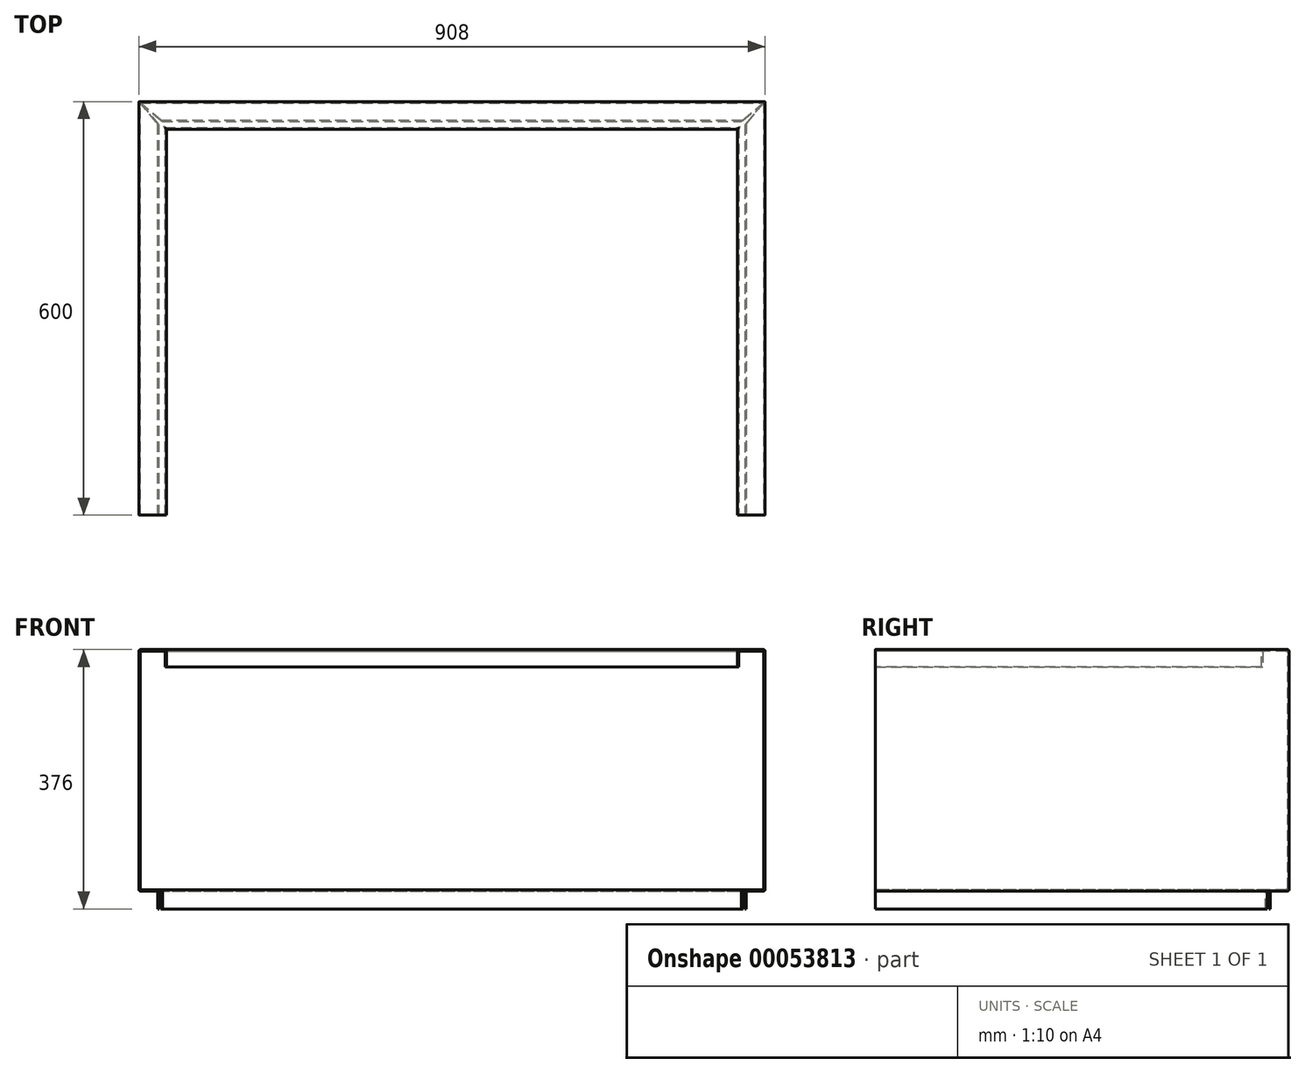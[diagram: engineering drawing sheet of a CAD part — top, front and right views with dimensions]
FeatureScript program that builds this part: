
annotation { "Feature Type Name" : "Feature", "Feature Type Description" : "" }
export const myFeature = defineFeature(function(context is Context, id is Id, definition is map)
    precondition{}
    {
        {
            var Q0;
            Q0=qCreatedBy(makeId("Front.planeOp"),FACE);
            var sketch = newSketch(context, id + "F0", { "sketchPlane" : qUnion([Q0])});
            skLineSegment(sketch, "E0", {"start": v(40, -25) * mm, "end": v(40, 0) * mm});
            skLineSegment(sketch, "E1", {"start": v(40, 0) * mm, "end": v(0, 0) * mm});
            skLineSegment(sketch, "E2", {"start": v(0, 0) * mm, "end": v(0, -350) * mm});
            skLineSegment(sketch, "E3", {"start": v(0, -350) * mm, "end": v(27, -350) * mm});
            skLineSegment(sketch, "E4", {"start": v(27, -350) * mm, "end": v(27, -376) * mm});
            skLineSegment(sketch, "E5.0", {"start": v(29, -348) * mm, "end": v(29, -376) * mm});
            skLineSegment(sketch, "E5.1", {"start": v(38, -25) * mm, "end": v(38, -2) * mm});
            skLineSegment(sketch, "E5.2", {"start": v(38, -2) * mm, "end": v(2, -2) * mm});
            skLineSegment(sketch, "E5.3", {"start": v(2, -2) * mm, "end": v(2, -348) * mm});
            skLineSegment(sketch, "E5.4", {"start": v(2, -348) * mm, "end": v(29, -348) * mm});
            skLineSegment(sketch, "E6", {"start": v(38, -25) * mm, "end": v(40, -25) * mm});
            skLineSegment(sketch, "E7", {"start": v(27, -376) * mm, "end": v(29, -376) * mm});
            skSolve(sketch);
        }
        {
            var Q0;
            Q0=qCreatedBy(makeId("Top.planeOp"),FACE);
            var sketch = newSketch(context, id + "F1", { "sketchPlane" : qUnion([Q0])});
            skLineSegment(sketch, "E8", {"start": v(0, 0) * mm, "end": v(0, 600) * mm});
            skLineSegment(sketch, "E9", {"start": v(0, 600) * mm, "end": v(908, 600) * mm});
            skLineSegment(sketch, "E10", {"start": v(908, 600) * mm, "end": v(908, 0) * mm});
            skSolve(sketch);
        }
        {
            var Q0;
            Q0 = qSketchRegion(id + "F0", true);
            var Q1;
            Q1 = qConstructionFilter(qBodyType(qCreatedBy(id + "F1" ,EDGE), BodyType.WIRE), ConstructionObject.NO);
            sweep(context, id + "F2", {"profiles" : qUnion([Q0]), "path" : qUnion([Q1])});
        }
        {
            var Q0;
            Q0=makeQuery(id+"F2.opSweep","SWEPT_FACE",FACE,{"disambiguationData":[OSD([sQuery(id+"F0.wireOp",EDGE,"E5.4"),sQuery(id+"F1.wireOp",EDGE,"E8")])]});
            var sketch = newSketch(context, id + "F3", { "sketchPlane" : qUnion([Q0])});
            skLineSegment(sketch, "E11", {"start": v(2, 598) * mm, "end": v(29, 565.82) * mm});
            skLineSegment(sketch, "E12", {"start": v(29, 565.82) * mm, "end": v(34.18, 571) * mm});
            skLineSegment(sketch, "E13", {"start": v(34.18, 571) * mm, "end": v(2, 598) * mm});
            skLineSegment(sketch, "E14", {"start": v(906, 598) * mm, "end": v(879, 565.82) * mm});
            skLineSegment(sketch, "E15", {"start": v(879, 565.82) * mm, "end": v(873.82, 571) * mm});
            skLineSegment(sketch, "E16", {"start": v(873.82, 571) * mm, "end": v(906, 598) * mm});
            skSolve(sketch);
        }
        {
            var Q0;
            {var subQ0=sQuery(id+"F3.wireOp",EDGE,"E14");Q0=makeQuery(id+"F3.imprint","IMPRINT",FACE,{"disambiguationData":[TD([[makeQuery(id+"F3.imprint","IMPRINT",EDGE,{"derivedFrom":subQ0}),-1.0]])]});}
            var Q1;
            {var subQ0=sQuery(id+"F3.wireOp",EDGE,"E11");Q1=makeQuery(id+"F3.imprint","IMPRINT",FACE,{"disambiguationData":[TD([[makeQuery(id+"F3.imprint","IMPRINT",EDGE,{"derivedFrom":subQ0}),1.0]])]});}
            extrude(context, id + "F4", {"entities" : qUnion([Q0, Q1]), "operationType" : NewBodyOperationType.REMOVE, "oppositeDirection" : true, "depth" : 30 * mm});
        }
        {
            var Q0;
            Q0=makeQuery(id+"F2.opSweep","SWEPT_EDGE",EDGE,{"disambiguationData":[OSD([sQuery(id+"F0.wireOp",EDGE,"E0"),sQuery(id+"F0.wireOp",EDGE,"E1"),sQuery(id+"F1.wireOp",EDGE,"E8")])]});
            var Q1;
            Q1=makeQuery(id+"F2.opSweep","SWEPT_EDGE",EDGE,{"disambiguationData":[OSD([sQuery(id+"F0.wireOp",EDGE,"E1"),sQuery(id+"F0.wireOp",EDGE,"E2"),sQuery(id+"F1.wireOp",EDGE,"E8")])]});
            var Q2;
            Q2=makeQuery(id+"F2.opSweep","SWEPT_EDGE",EDGE,{"disambiguationData":[OSD([sQuery(id+"F0.wireOp",EDGE,"E1"),sQuery(id+"F0.wireOp",EDGE,"E2"),sQuery(id+"F1.wireOp",EDGE,"E9")])]});
            var Q3;
            Q3=makeQuery(id+"F2.opSweep","SWEPT_EDGE",EDGE,{"disambiguationData":[OSD([sQuery(id+"F0.wireOp",EDGE,"E0"),sQuery(id+"F0.wireOp",EDGE,"E1"),sQuery(id+"F1.wireOp",EDGE,"E9")])]});
            var Q4;
            Q4=makeQuery(id+"F2.opSweep","SWEPT_EDGE",EDGE,{"disambiguationData":[OSD([sQuery(id+"F0.wireOp",EDGE,"E0"),sQuery(id+"F0.wireOp",EDGE,"E1"),sQuery(id+"F1.wireOp",EDGE,"E10")])]});
            var Q5;
            Q5=makeQuery(id+"F2.opSweep","SWEPT_EDGE",EDGE,{"disambiguationData":[OSD([sQuery(id+"F0.wireOp",EDGE,"E1"),sQuery(id+"F0.wireOp",EDGE,"E2"),sQuery(id+"F1.wireOp",EDGE,"E10")])]});
            var Q6;
            Q6=makeQuery(id+"F2.opSweep","SWEPT_EDGE",EDGE,{"disambiguationData":[OSD([sQuery(id+"F0.wireOp",EDGE,"E5.0"),sQuery(id+"F0.wireOp",EDGE,"E5.4"),sQuery(id+"F1.wireOp",EDGE,"E8")])]});
            var Q7;
            Q7=makeQuery(id+"F2.opSweep","SWEPT_EDGE",EDGE,{"disambiguationData":[OSD([sQuery(id+"F0.wireOp",EDGE,"E5.3"),sQuery(id+"F0.wireOp",EDGE,"E5.4"),sQuery(id+"F1.wireOp",EDGE,"E8")])]});
            var Q8;
            Q8=makeQuery(id+"F2.opSweep","SWEPT_EDGE",EDGE,{"disambiguationData":[OSD([sQuery(id+"F0.wireOp",EDGE,"E5.3"),sQuery(id+"F0.wireOp",EDGE,"E5.4"),sQuery(id+"F1.wireOp",EDGE,"E9")])]});
            var Q9;
            Q9=makeQuery(id+"F2.opSweep","SWEPT_EDGE",EDGE,{"disambiguationData":[OSD([sQuery(id+"F0.wireOp",EDGE,"E5.0"),sQuery(id+"F0.wireOp",EDGE,"E5.4"),sQuery(id+"F1.wireOp",EDGE,"E9")])]});
            var Q10;
            Q10=makeQuery(id+"F2.opSweep","SWEPT_EDGE",EDGE,{"disambiguationData":[OSD([sQuery(id+"F0.wireOp",EDGE,"E5.3"),sQuery(id+"F0.wireOp",EDGE,"E5.4"),sQuery(id+"F1.wireOp",EDGE,"E10")])]});
            var Q11;
            Q11=makeQuery(id+"F2.opSweep","SWEPT_EDGE",EDGE,{"disambiguationData":[OSD([sQuery(id+"F0.wireOp",EDGE,"E5.0"),sQuery(id+"F0.wireOp",EDGE,"E5.4"),sQuery(id+"F1.wireOp",EDGE,"E10")])]});
            var Q12;
            Q12=makeQuery(id+"F2.opSweep","SWEPT_EDGE",EDGE,{"disambiguationData":[OSD([sQuery(id+"F0.wireOp",EDGE,"E3"),sQuery(id+"F0.wireOp",EDGE,"E4"),sQuery(id+"F1.wireOp",EDGE,"E10")])]});
            var Q13;
            Q13=makeQuery(id+"F2.opSweep","SWEPT_EDGE",EDGE,{"disambiguationData":[OSD([sQuery(id+"F0.wireOp",EDGE,"E2"),sQuery(id+"F0.wireOp",EDGE,"E3"),sQuery(id+"F1.wireOp",EDGE,"E10")])]});
            var Q14;
            Q14=makeQuery(id+"F2.opSweep","SWEPT_EDGE",EDGE,{"disambiguationData":[OSD([sQuery(id+"F0.wireOp",EDGE,"E5.1"),sQuery(id+"F0.wireOp",EDGE,"E5.2"),sQuery(id+"F1.wireOp",EDGE,"E10")])]});
            var Q15;
            Q15=makeQuery(id+"F2.opSweep","SWEPT_EDGE",EDGE,{"disambiguationData":[OSD([sQuery(id+"F0.wireOp",EDGE,"E5.2"),sQuery(id+"F0.wireOp",EDGE,"E5.3"),sQuery(id+"F1.wireOp",EDGE,"E8")])]});
            var Q16;
            Q16=makeQuery(id+"F2.opSweep","SWEPT_EDGE",EDGE,{"disambiguationData":[OSD([sQuery(id+"F0.wireOp",EDGE,"E5.2"),sQuery(id+"F0.wireOp",EDGE,"E5.3"),sQuery(id+"F1.wireOp",EDGE,"E9")])]});
            var Q17;
            Q17=makeQuery(id+"F2.opSweep","SWEPT_EDGE",EDGE,{"disambiguationData":[OSD([sQuery(id+"F0.wireOp",EDGE,"E5.1"),sQuery(id+"F0.wireOp",EDGE,"E5.2"),sQuery(id+"F1.wireOp",EDGE,"E8")])]});
            var Q18;
            Q18=makeQuery(id+"F2.opSweep","SWEPT_EDGE",EDGE,{"disambiguationData":[OSD([sQuery(id+"F0.wireOp",EDGE,"E5.2"),sQuery(id+"F0.wireOp",EDGE,"E5.3"),sQuery(id+"F1.wireOp",EDGE,"E10")])]});
            var Q19;
            Q19=makeQuery(id+"F2.opSweep","SWEPT_EDGE",EDGE,{"disambiguationData":[OSD([sQuery(id+"F0.wireOp",EDGE,"E5.1"),sQuery(id+"F0.wireOp",EDGE,"E5.2"),sQuery(id+"F1.wireOp",EDGE,"E9")])]});
            var Q20;
            Q20=makeQuery(id+"F2.opSweep","SWEPT_EDGE",EDGE,{"disambiguationData":[OSD([sQuery(id+"F0.wireOp",EDGE,"E2"),sQuery(id+"F0.wireOp",EDGE,"E3"),sQuery(id+"F1.wireOp",EDGE,"E9")])]});
            var Q21;
            Q21=makeQuery(id+"F2.opSweep","SWEPT_EDGE",EDGE,{"disambiguationData":[OSD([sQuery(id+"F0.wireOp",EDGE,"E2"),sQuery(id+"F0.wireOp",EDGE,"E3"),sQuery(id+"F1.wireOp",EDGE,"E8")])]});
            var Q22;
            Q22=makeQuery(id+"F2.opSweep","SWEPT_EDGE",EDGE,{"disambiguationData":[OSD([sQuery(id+"F0.wireOp",EDGE,"E3"),sQuery(id+"F0.wireOp",EDGE,"E4"),sQuery(id+"F1.wireOp",EDGE,"E8")])]});
            var Q23;
            Q23=makeQuery(id+"F2.opSweep","SWEPT_EDGE",EDGE,{"disambiguationData":[OSD([sQuery(id+"F0.wireOp",EDGE,"E3"),sQuery(id+"F0.wireOp",EDGE,"E4"),sQuery(id+"F1.wireOp",EDGE,"E9")])]});
            fillet(context, id + "F5", {"entities" : qUnion([Q0, Q1, Q2, Q3, Q4, Q5, Q6, Q7, Q8, Q9, Q10, Q11, Q12, Q13, Q14, Q15, Q16, Q17, Q18, Q19, Q20, Q21, Q22, Q23]), "radius" : 2 * mm, "tangentPropagation" : true, "allowEdgeOverflow" : false});
        }
    });
